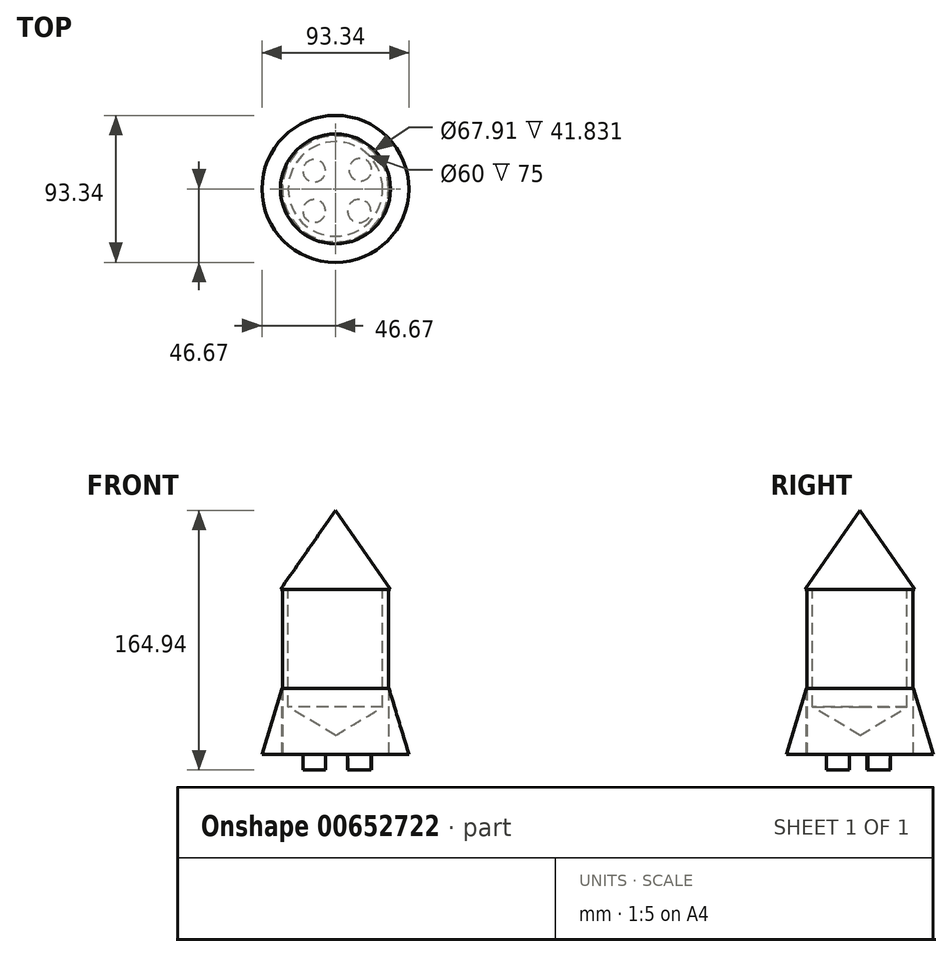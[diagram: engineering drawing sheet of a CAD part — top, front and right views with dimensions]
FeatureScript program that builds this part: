
annotation { "Feature Type Name" : "Feature", "Feature Type Description" : "" }
export const myFeature = defineFeature(function(context is Context, id is Id, definition is map)
    precondition{}
    {
        {
            var Q0;
            Q0=qCreatedBy(makeId("Top.planeOp"),FACE);
            var sketch = newSketch(context, id + "F0", { "sketchPlane" : qUnion([Q0])});
            skCircle(sketch, "E0", {"center": v(0, 0) * mm, "radius": 33.65 * mm});
            skSolve(sketch);
        }
        {
            var Q0;
            Q0 = qSketchRegion(id + "F0", true);
            extrude(context, id + "F1", {"entities" : qUnion([Q0]), "depth" : 105 * mm, "offsetDistance" : 25 * mm});
        }
        {
            var Q0;
            Q0=makeQuery(id+"F1.opExtrude","CAP_FACE",FACE,{"disambiguationData":[OSD([sQuery(id+"F0.wireOp",EDGE,"E0")])],"isStart":false});
            var sketch = newSketch(context, id + "F2", { "sketchPlane" : qUnion([Q0])});
            skPoint(sketch, "E1", {"position": v(0, 0) * mm});
            skSolve(sketch);
        }
        {
            var Q0;
            Q0=sQuery(id+"F2.wireOp",VERTEX,"E1");
            var Q1;
            Q1=makeQuery(id+"F1.opExtrude","SWEPT_BODY",BODY,{"disambiguationData":[OSD([sQuery(id+"F0.wireOp",EDGE,"E0")])]});
            hole(context, id + "F3", {"style" : HoleStyle.SIMPLE, "endStyle" : HoleEndStyle.BLIND, "holeDiameter" : 60 * mm, "majorDiameter" : 5 * mm, "holeDepth" : 75 * mm, "isTappedThrough" : true, "tappedDepth" : 12 * mm, "tapClearance" : 3, "locations" : qUnion([Q0]), "scope" : qUnion([Q1])});
        }
        {
            var Q0;
            Q0=qCreatedBy(makeId("Front.planeOp"),FACE);
            var sketch = newSketch(context, id + "F4", { "sketchPlane" : qUnion([Q0])});
            skLineSegment(sketch, "E2", {"start": v(0, 104.75) * mm, "end": v(0, 154.94) * mm});
            skLineSegment(sketch, "E3", {"start": v(0, 104.75) * mm, "end": v(-35.42, 104.75) * mm});
            skLineSegment(sketch, "E4", {"start": v(0, 154.94) * mm, "end": v(-34.9, 104.75) * mm});
            skSolve(sketch);
        }
        {
            var Q0;
            {var subQ0=sQuery(id+"F4.wireOp",EDGE,"E2");Q0=makeQuery(id+"F4.imprint","IMPRINT",FACE,{"disambiguationData":[TD([[makeQuery(id+"F4.imprint","IMPRINT",EDGE,{"derivedFrom":subQ0}),1.0]])]});}
            var Q1;
            Q1=makeQuery(id+"F1.opExtrude","CAP_EDGE",EDGE,{"disambiguationData":[OSD([sQuery(id+"F0.wireOp",EDGE,"E0")])],"isStart":false});
            revolve(context, id + "F5", {"entities" : qUnion([Q0]), "axis" : qUnion([Q1]), "revolveType" : RevolveType.FULL});
        }
        {
            var Q0;
            Q0=qCreatedBy(makeId("Right.planeOp"),FACE);
            var sketch = newSketch(context, id + "F6", { "sketchPlane" : qUnion([Q0])});
            skPoint(sketch, "E5", {"position": v(33.57, 0) * mm});
            skLineSegment(sketch, "E6", {"start": v(33.95, -0.13) * mm, "end": v(33.95, 41.83) * mm});
            skLineSegment(sketch, "E7", {"start": v(33.95, 41.83) * mm, "end": v(46.67, 0) * mm});
            skLineSegment(sketch, "E8", {"start": v(46.67, 0) * mm, "end": v(33.57, 0) * mm});
            skSolve(sketch);
        }
        {
            var Q0;
            {var subQ0=sQuery(id+"F6.wireOp",EDGE,"E7");Q0=makeQuery(id+"F6.imprint","IMPRINT",FACE,{"disambiguationData":[TD([[makeQuery(id+"F6.imprint","IMPRINT",EDGE,{"derivedFrom":subQ0}),-1.0]])]});}
            var Q1;
            Q1=makeQuery(id+"F1.opExtrude","SWEPT_FACE",FACE,{"disambiguationData":[OSD([sQuery(id+"F0.wireOp",EDGE,"E0")])]});
            revolve(context, id + "F7", {"entities" : qUnion([Q0]), "axis" : qUnion([Q1]), "revolveType" : RevolveType.FULL});
        }
        {
            var Q0;
            Q0=makeQuery(id+"F0.imprint","IMPRINT",FACE,{"disambiguationData":[TD([[makeQuery(id+"F0.imprint","IMPRINT",EDGE,{"derivedFrom":sQuery(id+"F0.wireOp",EDGE,"E0")}),1.0]])]});
            var sketch = newSketch(context, id + "F8", { "sketchPlane" : qUnion([Q0])});
            skCircle(sketch, "E9", {"center": v(15.08, -14.01) * mm, "radius": 7.38 * mm});
            skSolve(sketch);
        }
        {
            var Q0;
            Q0 = qSketchRegion(id + "F8", true);
            extrude(context, id + "F9", {"entities" : qUnion([Q0]), "operationType" : NewBodyOperationType.ADD, "oppositeDirection" : true, "depth" : 10 * mm, "offsetDistance" : 25 * mm});
        }
        {
            var Q0;
            Q0=makeQuery(id+"F0.imprint","IMPRINT",FACE,{"disambiguationData":[TD([[makeQuery(id+"F0.imprint","IMPRINT",EDGE,{"derivedFrom":sQuery(id+"F0.wireOp",EDGE,"E0")}),1.0]])]});
            var sketch = newSketch(context, id + "F10", { "sketchPlane" : qUnion([Q0])});
            skCircle(sketch, "E10", {"center": v(-13.54, 11.53) * mm, "radius": 7.16 * mm});
            skSolve(sketch);
        }
        {
            var Q0;
            Q0 = qSketchRegion(id + "F10", true);
            extrude(context, id + "F11", {"entities" : qUnion([Q0]), "operationType" : NewBodyOperationType.ADD, "oppositeDirection" : true, "depth" : 10 * mm, "offsetDistance" : 25 * mm});
        }
        {
            var Q0;
            Q0=makeQuery(id+"F0.imprint","IMPRINT",FACE,{"disambiguationData":[TD([[makeQuery(id+"F0.imprint","IMPRINT",EDGE,{"derivedFrom":sQuery(id+"F0.wireOp",EDGE,"E0")}),1.0]])]});
            var sketch = newSketch(context, id + "F12", { "sketchPlane" : qUnion([Q0])});
            skCircle(sketch, "E11", {"center": v(15.79, 12.24) * mm, "radius": 7.2 * mm});
            skSolve(sketch);
        }
        {
            var Q0;
            Q0 = qSketchRegion(id + "F12", true);
            extrude(context, id + "F13", {"entities" : qUnion([Q0]), "operationType" : NewBodyOperationType.ADD, "oppositeDirection" : true, "depth" : 10 * mm, "offsetDistance" : 25 * mm});
        }
        {
            var Q0;
            Q0=makeQuery(id+"F0.imprint","IMPRINT",FACE,{"disambiguationData":[TD([[makeQuery(id+"F0.imprint","IMPRINT",EDGE,{"derivedFrom":sQuery(id+"F0.wireOp",EDGE,"E0")}),1.0]])]});
            var sketch = newSketch(context, id + "F14", { "sketchPlane" : qUnion([Q0])});
            skCircle(sketch, "E12", {"center": v(-13.54, -14.01) * mm, "radius": 7.2 * mm});
            skSolve(sketch);
        }
        {
            var Q0;
            Q0 = qSketchRegion(id + "F14", true);
            extrude(context, id + "F15", {"entities" : qUnion([Q0]), "operationType" : NewBodyOperationType.ADD, "oppositeDirection" : true, "depth" : 10 * mm, "offsetDistance" : 25 * mm});
        }
    });
